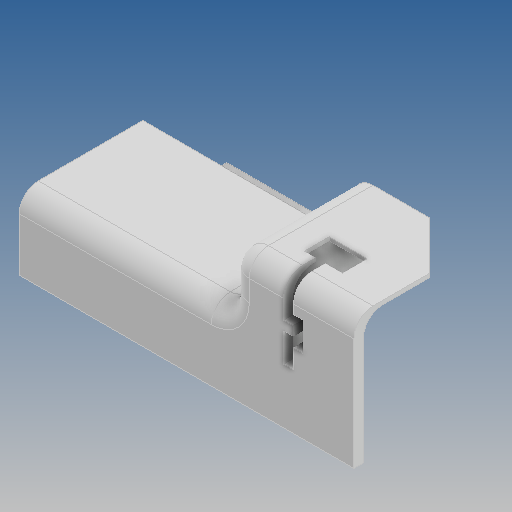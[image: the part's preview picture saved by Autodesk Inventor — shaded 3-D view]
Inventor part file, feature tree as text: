
AUTODESK INVENTOR PART (.ipt)
format: ipt  version: 2020 (Build 240168000, 168)  size: 247,296 bytes
history: native  units: mm
features: reference x14, extrude x7, sketch x7, fillet x3, other x2, direct_edit x1, move_body x1
ambient origin geometry x8: Origin, YZ Plane, XZ Plane, XY Plane, X Axis, Y Axis, Z Axis, Center Point
bodies: Solid1 (feature_tree)
feature tree (35):
  extrude  "Extrusion1"  Depth=69.0mm
  extrude  "Extrusion2"  TaperAngle=0.0deg  [1 undecoded]
  fillet  "Fillet1"  Radius=10.0mm
  extrude  "Extrusion3"  Depth=60.0mm TaperAngle=0.0deg
  extrude  "Extrusion4"  Depth=33.0mm
  extrude  "Extrusion5"  Depth=30.0mm
  extrude  "Extrusion6"  Depth=5.0mm
  fillet  "Fillet2"  Radius=10.0mm
  extrude  "Extrusion7"  Depth=15.0mm
  direct_edit  "Direct Edit1"
  fillet  "Fillet3"  Radius=10.0mm
  sketch  "Sketch1"  dims[d0=177.0mm d1=69.0mm]
  sketch  "Sketch2"  dims[d2=65.0mm d3=0.0mm d4=0.0mm d5=0.0mm d6=10.0mm]
  reference  "Reference2"
  reference  "Reference3"
  sketch  "Sketch3"  dims[d7=60.0mm d8=0.0mm d9=60.0mm d10=0.0mm]
  reference  "Reference4"
  reference  "Reference5"
  reference  "Reference6"
  sketch  "Sketch4"  dims[d11=5.0mm d13=33.0mm]
  sketch  "Sketch5"  dims[d14=30.0mm d15=0.0mm d17=0.15mm]
  sketch  "Sketch6"  dims[d18=8.0mm d19=0.0mm d20=5.0mm d21=10.0mm]
  reference  "Reference8"
  reference  "Reference9"
  reference  "Reference10"
  reference  "Reference11"
  reference  "Reference12"
  reference  "Reference13"
  reference  "Reference14"
  reference  "Reference15"
  reference  "Reference16"
  sketch  "Sketch7"  dims[d23=15.0mm d24=15.0mm d25=10.0mm d26=20.0mm d27=13.0mm d28=30.0mm d29=0.0mm d35=0.15mm d36=1.5mm d37=1.5mm d38=2.0mm d39=2.0mm d40=1.0mm d41=0.0mm d42=0.0mm d43=-1.0mm d44=10.0mm]
  other  "30-00 Injectomat suplimentar.iam"
  other  "0008-30-002 Corp_Injectomat1:1"
  move_body  "Move1"
note: 1 required parameter value undecoded (feature->parameter linkage not recoverable at this tier; creation-order binding heuristic only, values carry confidence <= 0.55)
